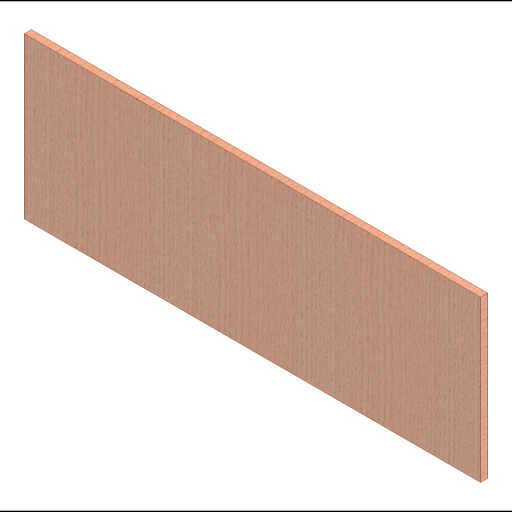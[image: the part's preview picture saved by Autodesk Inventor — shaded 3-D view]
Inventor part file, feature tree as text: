
AUTODESK INVENTOR PART (.ipt)
format: ipt  version: 2023 (Build 270158000, 158)  size: 255,488 bytes
history: native  units: in
note: dims shown in document units (in); Inventor stores cm internally (conversion verified against a paired STEP export)
features: extrude x1, sketch x1
ambient origin geometry x8: Origin, YZ Plane, XZ Plane, XY Plane, X Axis, Y Axis, Z Axis, Center Point
bodies: Solid1 (feature_tree)
feature tree (2):
  extrude  "Extrusion1"  Depth=11.25in
  sketch  "Sketch1"  dims[d0=32.0in d1=11.25in d2=0.5in d3=0.0in]
